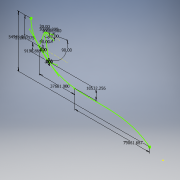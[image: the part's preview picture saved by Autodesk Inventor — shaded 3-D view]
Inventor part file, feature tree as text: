
AUTODESK INVENTOR PART (.ipt)
format: ipt  version: 2019 (Build 230136000, 136)  size: 109,568 bytes
history: native  units: in
note: dims shown in document units (in); Inventor stores cm internally (conversion verified against a paired STEP export)
features: sketch x2
ambient origin geometry x8: Origin, YZ Plane, XZ Plane, XY Plane, X Axis, Y Axis, Z Axis, Center Point
feature tree (2):
  sketch  "Sketch1"  dims[d21=21101.375in]
  sketch  "Sketch2"  dims[d22=37681.0in d23=79061.6875in d24=54945.8125in d25=0.1374in d27=0.0in d28=0.0in d30=90.0deg d31=10000.0in d35=10000.0in d37=90.0deg d38=9198.8693in d39=10532.2555in d40=0.0in d41=0.0in d42=0.0in d43=0.0687in]
